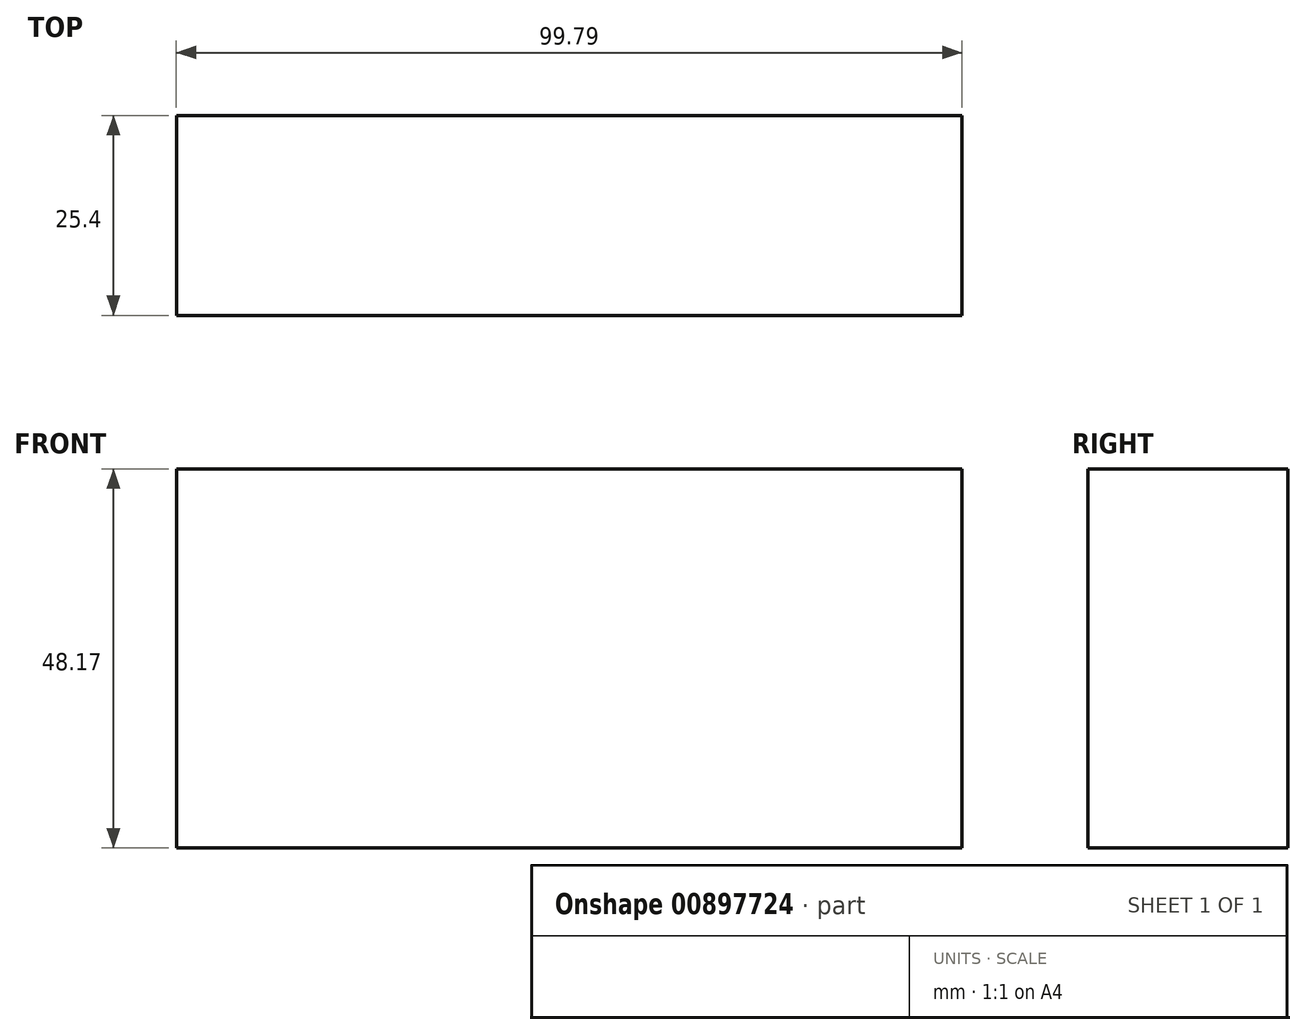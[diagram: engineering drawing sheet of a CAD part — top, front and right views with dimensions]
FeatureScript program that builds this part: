
annotation { "Feature Type Name" : "Feature", "Feature Type Description" : "" }
export const myFeature = defineFeature(function(context is Context, id is Id, definition is map)
    precondition{}
    {
        {
            var Q0;
            Q0=qCreatedBy(makeId("Front.planeOp"),FACE);
            var sketch = newSketch(context, id + "F0", { "sketchPlane" : qUnion([Q0])});
            skLineSegment(sketch, "E0.bottom", {"start": v(-43.76, 48.17) * mm, "end": v(56.03, 48.17) * mm});
            skLineSegment(sketch, "E0.top", {"start": v(-43.76, 0) * mm, "end": v(56.03, 0) * mm});
            skLineSegment(sketch, "E0.left", {"start": v(-43.76, 48.17) * mm, "end": v(-43.76, 0) * mm});
            skLineSegment(sketch, "E0.right", {"start": v(56.03, 48.17) * mm, "end": v(56.03, 0) * mm});
            skSolve(sketch);
        }
        {
            var Q0;
            Q0=makeQuery(id+"F0.imprint","IMPRINT",FACE,{"disambiguationData":[TD([[makeQuery(id+"F0.imprint","IMPRINT",EDGE,{"derivedFrom":sQuery(id+"F0.wireOp",EDGE,"E0.bottom")}),-1.0]])]});
            extrude(context, id + "F1", {"entities" : qUnion([Q0]), "depth" : 25.4 * mm, "offsetDistance" : 25.4 * mm});
        }
    });
